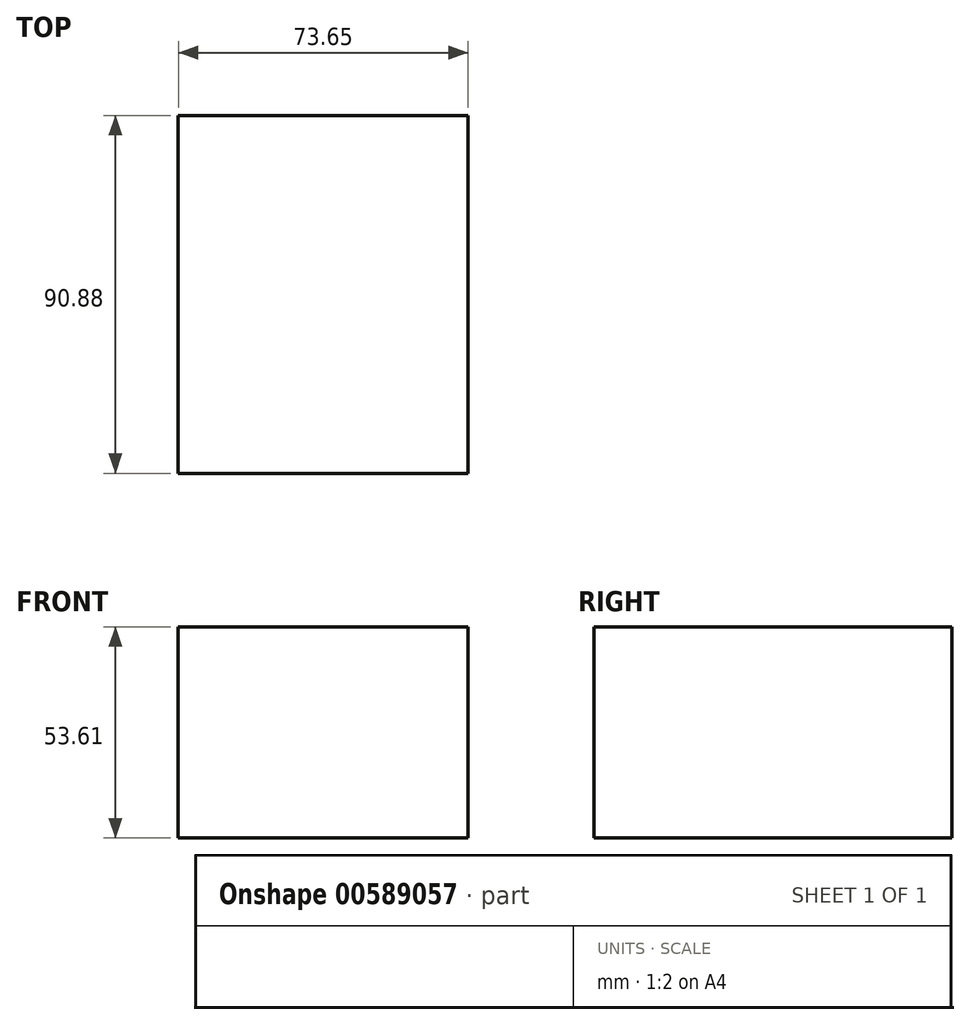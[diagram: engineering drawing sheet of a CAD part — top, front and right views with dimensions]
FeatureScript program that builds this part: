
annotation { "Feature Type Name" : "Feature", "Feature Type Description" : "" }
export const myFeature = defineFeature(function(context is Context, id is Id, definition is map)
    precondition{}
    {
        {
            var Q0;
            Q0=qCreatedBy(makeId("Front.planeOp"),FACE);
            var sketch = newSketch(context, id + "F0", { "sketchPlane" : qUnion([Q0])});
            skLineSegment(sketch, "E0.bottom", {"start": v(0, 0) * mm, "end": v(0, 0) * mm});
            skLineSegment(sketch, "E0.top", {"start": v(0, 0) * mm, "end": v(0, 0) * mm});
            skLineSegment(sketch, "E0.left", {"start": v(0, 0) * mm, "end": v(0, 0) * mm});
            skLineSegment(sketch, "E0.right", {"start": v(0, 0) * mm, "end": v(0, 0) * mm});
            skPoint(sketch, "E0.middle", {"position": v(0, 0) * mm});
            skLineSegment(sketch, "E1.bottom", {"start": v(27.68, 26.57) * mm, "end": v(-45.97, 26.57) * mm});
            skLineSegment(sketch, "E1.top", {"start": v(27.68, -27.04) * mm, "end": v(-45.97, -27.04) * mm});
            skLineSegment(sketch, "E1.left", {"start": v(27.68, 26.57) * mm, "end": v(27.68, -27.04) * mm});
            skLineSegment(sketch, "E1.right", {"start": v(-45.97, 26.57) * mm, "end": v(-45.97, -27.04) * mm});
            skSolve(sketch);
        }
        {
            var Q0;
            Q0 = qSketchRegion(id + "F0", true);
            extrude(context, id + "F1", {"entities" : qUnion([Q0]), "depth" : 90.88 * mm, "offsetDistance" : 25.4 * mm});
        }
    });
